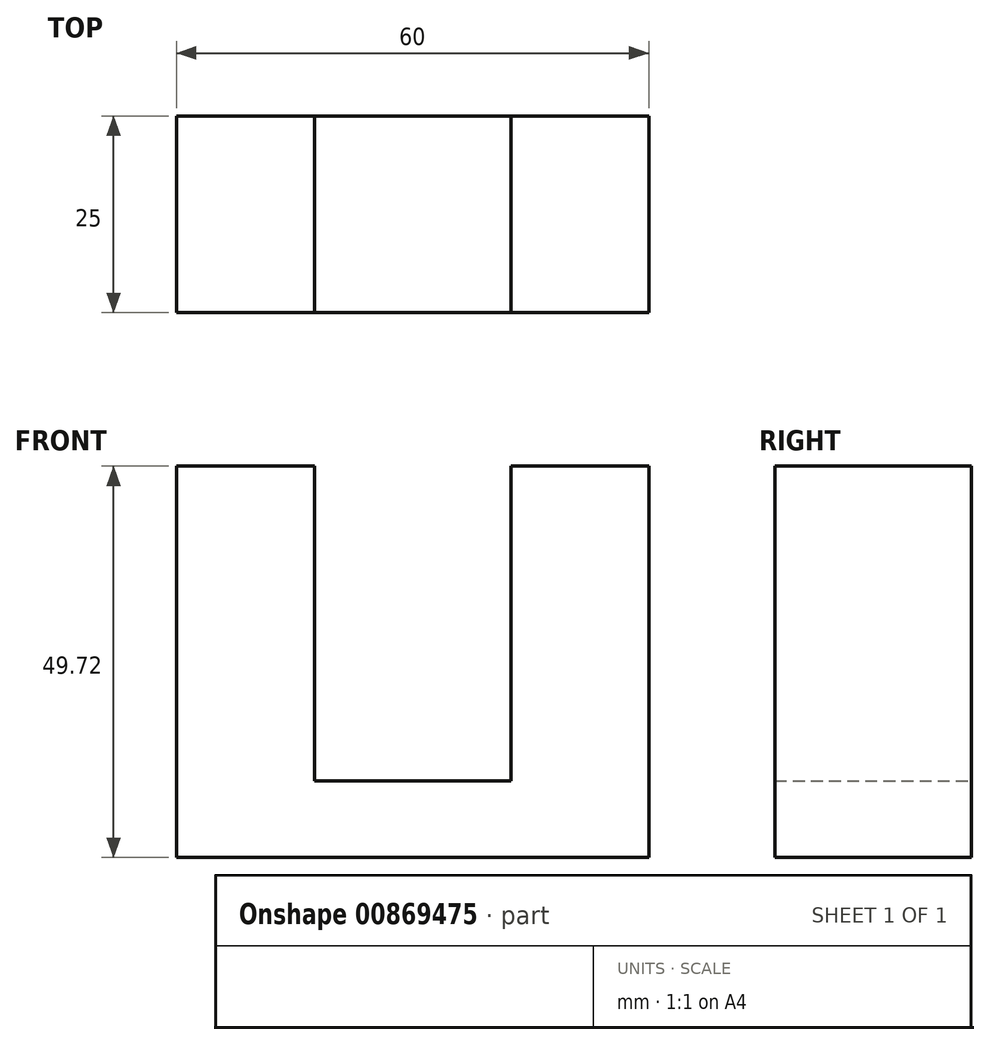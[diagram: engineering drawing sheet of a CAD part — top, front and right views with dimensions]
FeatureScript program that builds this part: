
annotation { "Feature Type Name" : "Feature", "Feature Type Description" : "" }
export const myFeature = defineFeature(function(context is Context, id is Id, definition is map)
    precondition{}
    {
        {
            var Q0;
            Q0=qCreatedBy(makeId("Front.planeOp"),FACE);
            var sketch = newSketch(context, id + "F0", { "sketchPlane" : qUnion([Q0])});
            skLineSegment(sketch, "E0", {"start": v(-34.45, 26.93) * mm, "end": v(-16.95, 26.93) * mm});
            skLineSegment(sketch, "E1", {"start": v(-16.95, 26.93) * mm, "end": v(-16.95, -13.07) * mm});
            skLineSegment(sketch, "E2", {"start": v(-16.95, -13.07) * mm, "end": v(8.05, -13.07) * mm});
            skLineSegment(sketch, "E3", {"start": v(8.05, -13.07) * mm, "end": v(8.05, 26.93) * mm});
            skLineSegment(sketch, "E4", {"start": v(8.05, 26.93) * mm, "end": v(25.55, 26.93) * mm});
            skLineSegment(sketch, "E5", {"start": v(25.55, 26.93) * mm, "end": v(25.55, -22.79) * mm});
            skLineSegment(sketch, "E6", {"start": v(25.55, -22.79) * mm, "end": v(-34.45, -22.79) * mm});
            skLineSegment(sketch, "E7", {"start": v(-34.45, -22.79) * mm, "end": v(-34.45, 26.93) * mm});
            skSolve(sketch);
        }
        {
            var Q0;
            Q0=makeQuery(id+"F0.imprint","IMPRINT",FACE,{"disambiguationData":[TD([[makeQuery(id+"F0.imprint","IMPRINT",EDGE,{"derivedFrom":sQuery(id+"F0.wireOp",EDGE,"E0")}),-1.0]])]});
            extrude(context, id + "F1", {"entities" : qUnion([Q0]), "endBound" : BoundingType.SYMMETRIC, "depth" : 25 * mm, "offsetDistance" : 25 * mm});
        }
    });
